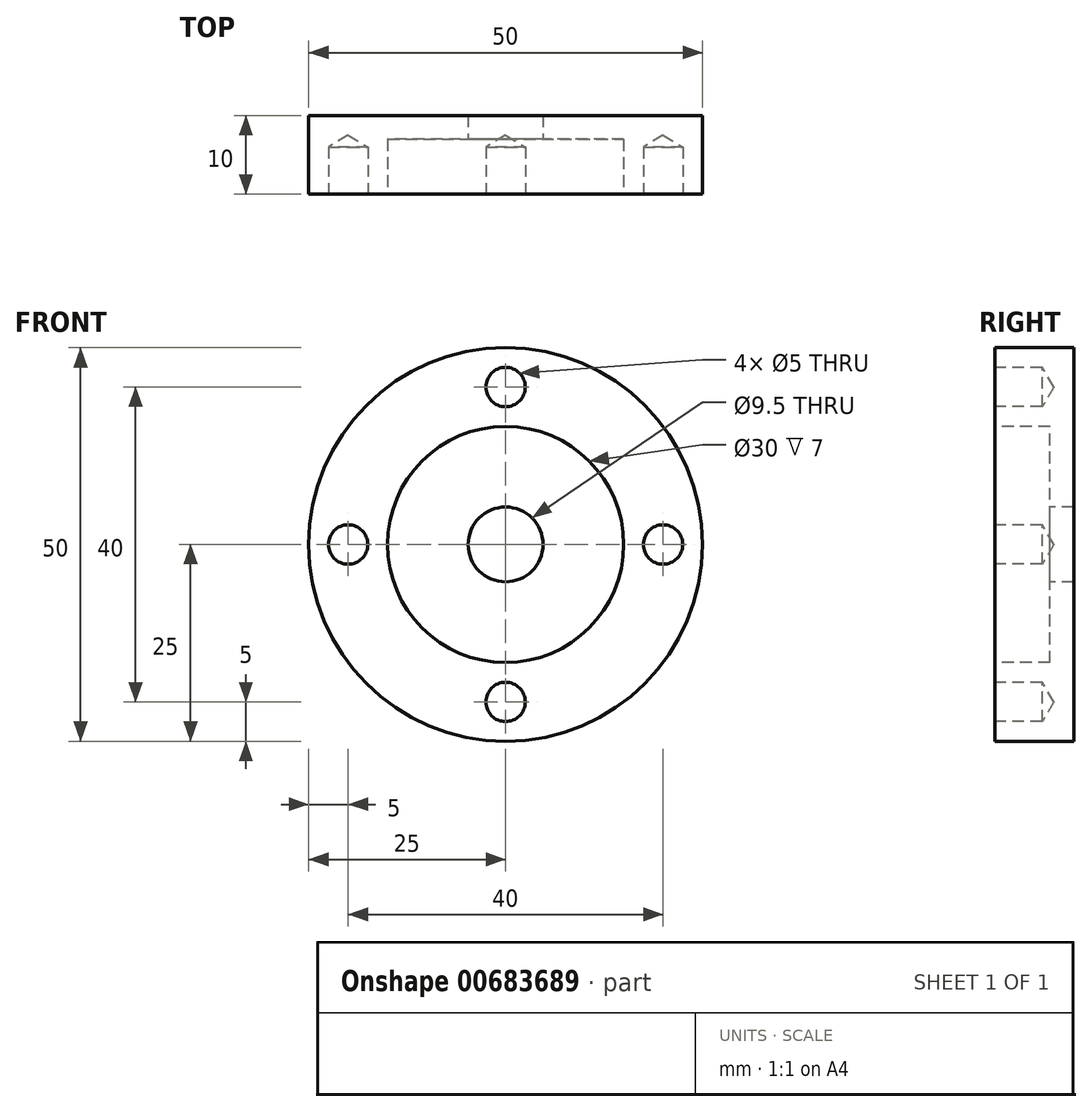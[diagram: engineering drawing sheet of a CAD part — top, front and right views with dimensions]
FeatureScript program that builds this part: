
annotation { "Feature Type Name" : "Feature", "Feature Type Description" : "" }
export const myFeature = defineFeature(function(context is Context, id is Id, definition is map)
    precondition{}
    {
        {
            var Q0;
            Q0=qCreatedBy(makeId("Front.planeOp"),FACE);
            var sketch = newSketch(context, id + "F0", { "sketchPlane" : qUnion([Q0])});
            skCircle(sketch, "E0", {"center": v(0, 0) * mm, "radius": 25 * mm});
            skSolve(sketch);
        }
        {
            var Q0;
            Q0 = qSketchRegion(id + "F0", true);
            extrude(context, id + "F1", {"entities" : qUnion([Q0]), "depth" : 10 * mm, "offsetDistance" : 25 * mm});
        }
        {
            var Q0;
            Q0=makeQuery(id+"F1.opExtrude","CAP_FACE",FACE,{"disambiguationData":[OSD([sQuery(id+"F0.wireOp",EDGE,"E0")])],"isStart":false});
            var sketch = newSketch(context, id + "F2", { "sketchPlane" : qUnion([Q0])});
            skCircle(sketch, "E1", {"center": v(0, 0) * mm, "radius": 4.75 * mm});
            skSolve(sketch);
        }
        {
            var Q0;
            Q0 = qSketchRegion(id + "F2", true);
            extrude(context, id + "F3", {"entities" : qUnion([Q0]), "operationType" : NewBodyOperationType.REMOVE, "oppositeDirection" : true, "depth" : 25 * mm, "offsetDistance" : 25 * mm});
        }
        {
            var Q0;
            Q0=makeQuery(id+"F1.opExtrude","CAP_FACE",FACE,{"disambiguationData":[OSD([sQuery(id+"F0.wireOp",EDGE,"E0")])],"isStart":false});
            var sketch = newSketch(context, id + "F4", { "sketchPlane" : qUnion([Q0])});
            skCircle(sketch, "E2", {"center": v(0, 0) * mm, "radius": 15 * mm});
            skSolve(sketch);
        }
        {
            var Q0;
            Q0 = qSketchRegion(id + "F4", true);
            extrude(context, id + "F5", {"entities" : qUnion([Q0]), "operationType" : NewBodyOperationType.REMOVE, "oppositeDirection" : true, "depth" : 7 * mm, "offsetDistance" : 25 * mm});
        }
        {
            var Q0;
            Q0=makeQuery(id+"F1.opExtrude","CAP_FACE",FACE,{"disambiguationData":[OSD([sQuery(id+"F0.wireOp",EDGE,"E0")])],"isStart":false});
            var sketch = newSketch(context, id + "F6", { "sketchPlane" : qUnion([Q0])});
            skCircle(sketch, "E3", {"center": v(0, 0) * mm, "radius": 20 * mm});
            skPoint(sketch, "E4", {"position": v(0, 20) * mm});
            skPoint(sketch, "E5.1.0", {"position": v(-20, 0) * mm});
            skPoint(sketch, "E5.2.0", {"position": v(0, -20) * mm});
            skPoint(sketch, "E5.3.0", {"position": v(20, 0) * mm});
            skSolve(sketch);
        }
        {
            var Q0;
            Q0=sQuery(id+"F6.wireOp",VERTEX,"E4");
            var Q1;
            Q1=sQuery(id+"F6.wireOp",VERTEX,"E5.3.0");
            var Q2;
            Q2=sQuery(id+"F6.wireOp",VERTEX,"E5.2.0");
            var Q3;
            Q3=sQuery(id+"F6.wireOp",VERTEX,"E5.1.0");
            var Q4;
            Q4=makeQuery(id+"F1.opExtrude","SWEPT_BODY",BODY,{"disambiguationData":[OSD([sQuery(id+"F0.wireOp",EDGE,"E0")])]});
            hole(context, id + "F7", {"style" : HoleStyle.SIMPLE, "endStyle" : HoleEndStyle.BLIND, "holeDiameter" : 5 * mm, "majorDiameter" : 5 * mm, "holeDepth" : 6 * mm, "isTappedThrough" : true, "tappedDepth" : 12 * mm, "tapClearance" : 3, "locations" : qUnion([Q0, Q1, Q2, Q3]), "scope" : qUnion([Q4])});
        }
    });
